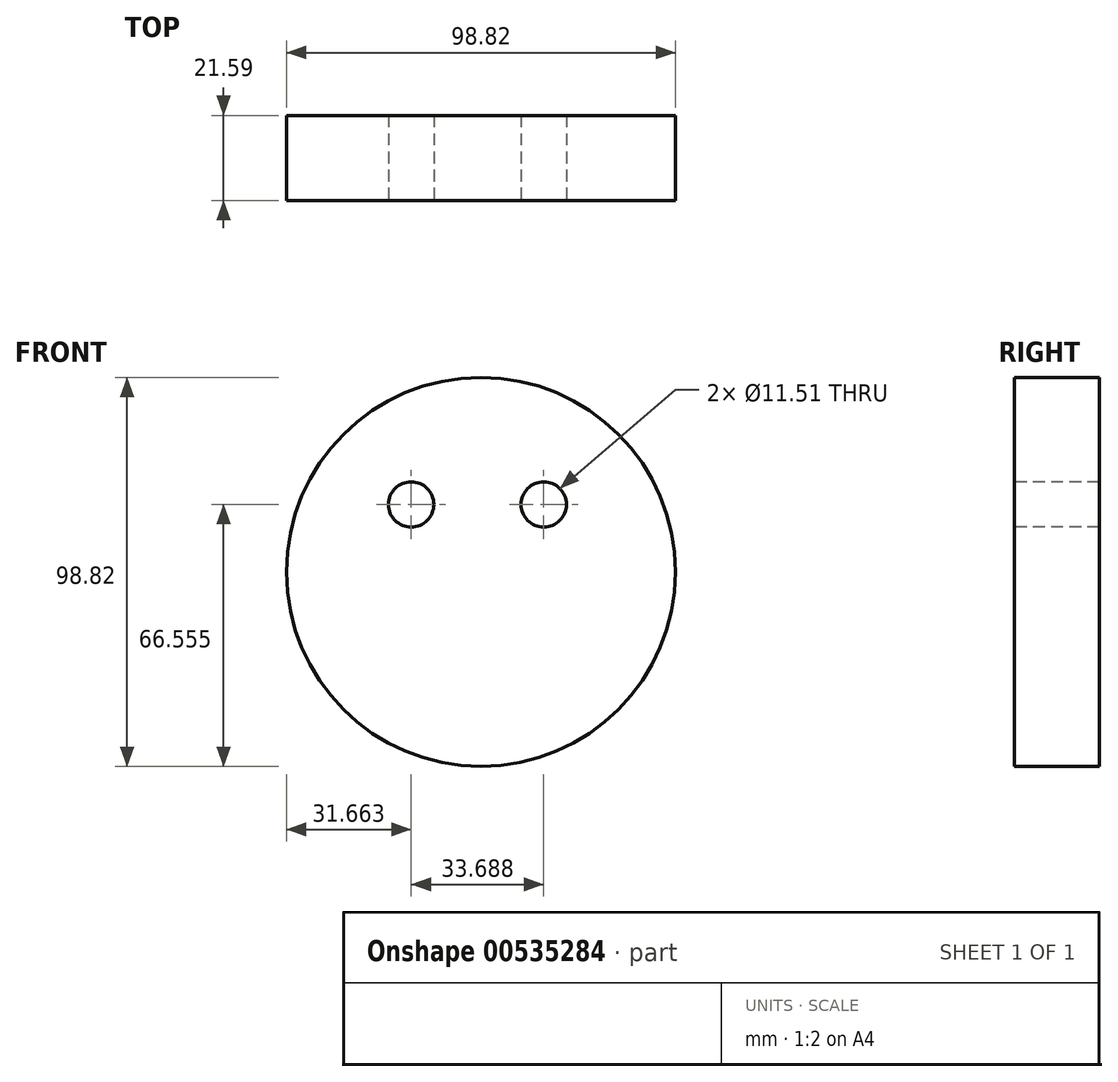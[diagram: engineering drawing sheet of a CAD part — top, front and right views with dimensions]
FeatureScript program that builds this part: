
annotation { "Feature Type Name" : "Feature", "Feature Type Description" : "" }
export const myFeature = defineFeature(function(context is Context, id is Id, definition is map)
    precondition{}
    {
        {
            var Q0;
            Q0=qCreatedBy(makeId("Front.planeOp"),FACE);
            var sketch = newSketch(context, id + "F0", { "sketchPlane" : qUnion([Q0])});
            skCircle(sketch, "E0", {"center": v(0, 0) * mm, "radius": 49.4 * mm});
            skSolve(sketch);
        }
        {
            var Q0;
            Q0=makeQuery(id+"F0.imprint","IMPRINT",FACE,{"disambiguationData":[TD([[makeQuery(id+"F0.imprint","IMPRINT",EDGE,{"derivedFrom":sQuery(id+"F0.wireOp",EDGE,"E0")}),1.0]])]});
            extrude(context, id + "F1", {"entities" : qUnion([Q0]), "depth" : 21.59 * mm, "offsetDistance" : 25.4 * mm});
        }
        {
            var Q0;
            Q0=makeQuery(id+"F1.opExtrude","CAP_FACE",FACE,{"disambiguationData":[OSD([sQuery(id+"F0.wireOp",EDGE,"E0")])],"isStart":false});
            var sketch = newSketch(context, id + "F2", { "sketchPlane" : qUnion([Q0])});
            skCircle(sketch, "E1", {"center": v(-17.75, 17.15) * mm, "radius": 7.79 * mm});
            skCircle(sketch, "E2", {"center": v(16.54, 16.84) * mm, "radius": 7.79 * mm});
            skSolve(sketch);
        }
        {
            var Q0;
            Q0=sQuery(id+"F2.wireOp",VERTEX,"E1.center");
            var Q1;
            Q1=makeQuery(id+"F1.opExtrude","SWEPT_BODY",BODY,{"disambiguationData":[OSD([sQuery(id+"F0.wireOp",EDGE,"E0")])]});
            hole(context, id + "F3", {"style" : HoleStyle.SIMPLE, "endStyle" : HoleEndStyle.THROUGH, "standardTappedOrClearance" : lookupTablePath({ "standard" : "ANSI", "fit" : "Close", "size" : "7/16", "type" : "Clearance" }), "standardBlindInLast" : lookupTablePath({ "fit" : "Close", "standard" : "ANSI", "size" : "7/16", "type" : "Clearance" }), "holeDiameter" : 11.5 * mm, "isTappedThrough" : true, "tappedDepth" : 12.7 * mm, "tapClearance" : 3, "locations" : qUnion([Q0]), "scope" : qUnion([Q1])});
        }
        {
            var Q0;
            Q0=makeQuery(id+"F1.opExtrude","CAP_FACE",FACE,{"disambiguationData":[OSD([sQuery(id+"F0.wireOp",EDGE,"E0")])],"isStart":false});
            var sketch = newSketch(context, id + "F4", { "sketchPlane" : qUnion([Q0])});
            skCircle(sketch, "E3", {"center": v(15.34, 17.15) * mm, "radius": 5.96 * mm});
            skSolve(sketch);
        }
        {
            var Q0;
            Q0=makeQuery(id+"F4.imprint","IMPRINT",FACE,{"disambiguationData":[TD([[makeQuery(id+"F4.imprint","IMPRINT",EDGE,{"derivedFrom":sQuery(id+"F4.wireOp",EDGE,"E3")}),-1.0]])]});
            var sketch = newSketch(context, id + "F5", { "sketchPlane" : qUnion([Q0])});
            skLineSegment(sketch, "E4", {"start": v(-17.75, 17.15) * mm, "end": v(15.94, 17.15) * mm});
            skCircle(sketch, "E5", {"center": v(15.94, 17.15) * mm, "radius": 6.87 * mm});
            skSolve(sketch);
        }
        {
            var Q0;
            Q0=sQuery(id+"F5.wireOp",VERTEX,"E4.end");
            var Q1;
            Q1=makeQuery(id+"F1.opExtrude","SWEPT_BODY",BODY,{"disambiguationData":[OSD([sQuery(id+"F0.wireOp",EDGE,"E0")])]});
            hole(context, id + "F6", {"style" : HoleStyle.SIMPLE, "endStyle" : HoleEndStyle.THROUGH, "standardTappedOrClearance" : lookupTablePath({ "standard" : "ANSI", "fit" : "Close", "size" : "7/16", "type" : "Clearance" }), "standardBlindInLast" : lookupTablePath({ "fit" : "Close", "standard" : "ANSI", "size" : "7/16", "type" : "Clearance" }), "holeDiameter" : 11.5 * mm, "isTappedThrough" : true, "tappedDepth" : 12.7 * mm, "tapClearance" : 3, "locations" : qUnion([Q0]), "scope" : qUnion([Q1])});
        }
    });
